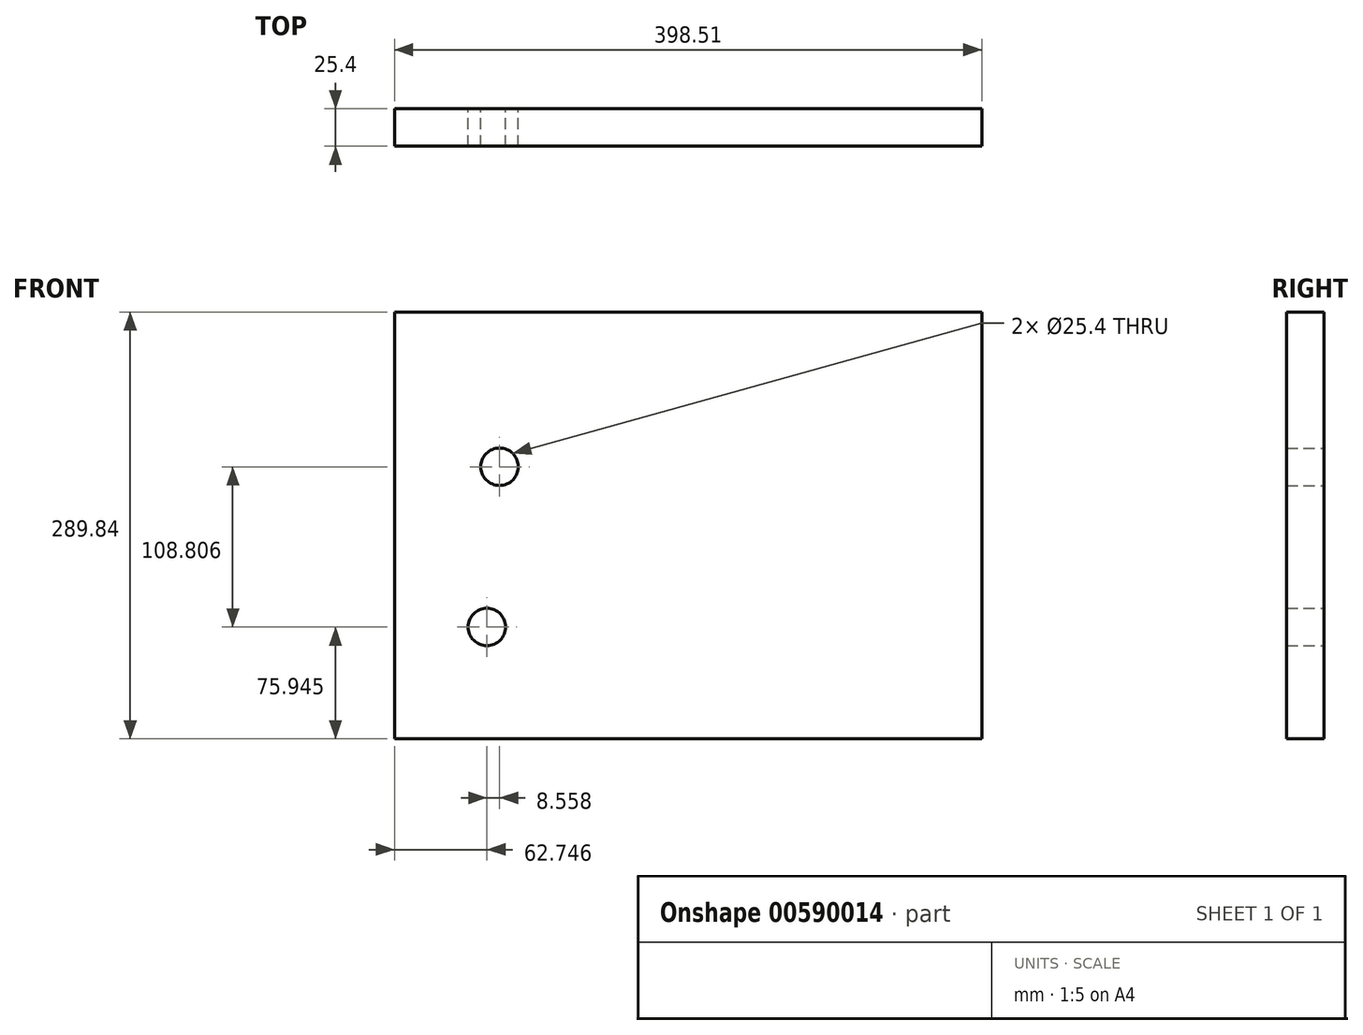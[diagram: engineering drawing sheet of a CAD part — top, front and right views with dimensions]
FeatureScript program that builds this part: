
annotation { "Feature Type Name" : "Feature", "Feature Type Description" : "" }
export const myFeature = defineFeature(function(context is Context, id is Id, definition is map)
    precondition{}
    {
        {
            var Q0;
            Q0=qCreatedBy(makeId("Front.planeOp"),FACE);
            var sketch = newSketch(context, id + "F0", { "sketchPlane" : qUnion([Q0])});
            skLineSegment(sketch, "E0.bottom", {"start": v(0, 0) * mm, "end": v(398.51, 0) * mm});
            skLineSegment(sketch, "E0.top", {"start": v(0, -289.84) * mm, "end": v(398.51, -289.84) * mm});
            skLineSegment(sketch, "E0.left", {"start": v(0, 0) * mm, "end": v(0, -289.84) * mm});
            skLineSegment(sketch, "E0.right", {"start": v(398.51, 0) * mm, "end": v(398.51, -289.84) * mm});
            skSolve(sketch);
        }
        {
            var Q0;
            Q0=makeQuery(id+"F0.imprint","IMPRINT",FACE,{"disambiguationData":[TD([[makeQuery(id+"F0.imprint","IMPRINT",EDGE,{"derivedFrom":sQuery(id+"F0.wireOp",EDGE,"E0.bottom")}),-1.0]])]});
            extrude(context, id + "F1", {"entities" : qUnion([Q0]), "depth" : 25.4 * mm, "offsetDistance" : 25.4 * mm});
        }
        {
            var Q0;
            Q0=makeQuery(id+"F1.opExtrude","CAP_FACE",FACE,{"disambiguationData":[OSD([sQuery(id+"F0.wireOp",EDGE,"E0.bottom"),sQuery(id+"F0.wireOp",EDGE,"E0.top"),sQuery(id+"F0.wireOp",EDGE,"E0.left"),sQuery(id+"F0.wireOp",EDGE,"E0.right")])],"isStart":true});
            var sketch = newSketch(context, id + "F2", { "sketchPlane" : qUnion([Q0])});
            skPoint(sketch, "E1", {"position": v(-62.75, -213.9) * mm});
            skPoint(sketch, "E2", {"position": v(-71.3, -105.09) * mm});
            skPoint(sketch, "E3", {"position": v(0, -119.23) * mm});
            skSolve(sketch);
        }
        {
            var Q0;
            Q0=sQuery(id+"F2.wireOp",VERTEX,"E2");
            var Q1;
            Q1=sQuery(id+"F2.wireOp",VERTEX,"E1");
            var Q2;
            Q2=makeQuery(id+"F1.opExtrude","SWEPT_BODY",BODY,{"disambiguationData":[OSD([sQuery(id+"F0.wireOp",EDGE,"E0.bottom"),sQuery(id+"F0.wireOp",EDGE,"E0.top"),sQuery(id+"F0.wireOp",EDGE,"E0.left"),sQuery(id+"F0.wireOp",EDGE,"E0.right")])]});
            hole(context, id + "F3", {"style" : HoleStyle.SIMPLE, "endStyle" : HoleEndStyle.THROUGH, "holeDiameter" : 25.4 * mm, "majorDiameter" : 6.35 * mm, "isTappedThrough" : true, "tappedDepth" : 12.7 * mm, "tapClearance" : 3, "locations" : qUnion([Q0, Q1]), "scope" : qUnion([Q2])});
        }
    });
